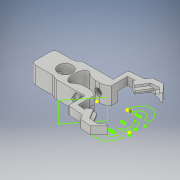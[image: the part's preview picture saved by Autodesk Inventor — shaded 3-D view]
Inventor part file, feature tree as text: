
AUTODESK INVENTOR PART (.ipt)
format: ipt  version: 2017 (Build 210142000, 142)  size: 1,308,160 bytes
history: native  units: in
note: dims shown in document units (in); Inventor stores cm internally (conversion verified against a paired STEP export)
features: sketch x38, projected_geometry x37, extrude x32, chamfer x8, plane x8, fillet x4, mirror x4, boolean_combine x3, move_body x3, split x2, revolve x1
ambient origin geometry x8: Origin, YZ Plane, XZ Plane, XY Plane, X Axis, Y Axis, Z Axis, Center Point
bodies: Solid2 (feature_tree), Solid4 (feature_tree), Solid5 (feature_tree), Solid6 (feature_tree), Solid7 (feature_tree), Solid8 (feature_tree)
feature tree (140):
  extrude  "Extrusion11"  Depth=0.1125in
  extrude  "Extrusion12"  Depth=0.0205in TaperAngle=0.0deg
  chamfer  "Chamfer17"  Distance=0.0627in Angle=45.0deg
  chamfer  "Chamfer18"  Distance=0.0627in Angle=45.0deg
  chamfer  "Chamfer19"  Distance=0.0627in Angle=45.0deg
  chamfer  "Chamfer20"  Distance=0.0627in Angle=45.0deg
  extrude  "Extrusion13"  Depth=0.0205in TaperAngle=0.0deg
  extrude  "Extrusion14"  Depth=0.0627in TaperAngle=45.0deg
  extrude  "Extrusion15"  Depth=0.0627in TaperAngle=45.0deg
  chamfer  "Chamfer21"  Distance=0.0627in Angle=45.0deg
  chamfer  "Chamfer22"  Distance=0.125in
  chamfer  "Chamfer23"  Distance=1.0in
  chamfer  "Chamfer24"  Distance=0.03in
  extrude  "Extrusion16"  Depth=0.03in
  fillet  "Fillet1"  [1 undecoded]
  extrude  "Extrusion17"  TaperAngle=90.0deg  [1 undecoded]
  fillet  "Fillet2"  Radius=0.03in
  extrude  "Extrusion18"  Depth=0.3in TaperAngle=0.0deg
  extrude  "Extrusion19"  Depth=1.0in TaperAngle=0.0deg
  extrude  "Extrusion22"  TaperAngle=90.0deg  [1 undecoded]
  extrude  "Extrusion25"  Depth=0.01in
  extrude  "Extrusion26"  Depth=0.5in
  revolve  "Revolution1"  [1 undecoded]
  plane  "Work Plane1"
  sketch  "Sketch33"  dims[d175=0.04in d176=1.0in d177=0.0in]
  sketch  "Sketch34"  dims[d179=0.06in d180=90.0deg]
  extrude  "Extrusion28"  Depth=0.185in TaperAngle=0.0deg
  boolean_combine  "Combine1"
  sketch  "Sketch35"  dims[d181=120.0deg d182=0.01in]
  plane  "Work Plane2"
  mirror  "Mirror1"
  extrude  "Extrusion29"  Depth=0.4119in TaperAngle=0.0deg
  extrude  "Extrusion30"  Depth=1.0in TaperAngle=0.0deg
  extrude  "Extrusion31"  Depth=0.13in
  extrude  "Extrusion32"  [1 undecoded]
  extrude  "Extrusion33"  Depth=0.13in TaperAngle=0.0deg
  extrude  "Extrusion34"  Depth=10.0in TaperAngle=0.0deg
  plane  "Work Plane3"
  extrude  "Extrusion35"  Depth=10.0in TaperAngle=0.0deg
  sketch  "Sketch44"  dims[d206=0.5in d207=0.0in d208=-0.12in]
  plane  "Work Plane5"
  split  "Split1"
  sketch  "Sketch45"  dims[d209=0.12in d210=0.13in d211=0.13in d212=0.0in]
  extrude  "Extrusion37"  Depth=10.0in TaperAngle=0.0deg
  move_body  "Move Body1"
  extrude  "Extrusion38"  Depth=0.1181in TaperAngle=0.0deg
  extrude  "Extrusion39"  Depth=0.1575in TaperAngle=0.0deg
  mirror  "Mirror2"
  extrude  "Extrusion40"  TaperAngle=90.0deg  [1 undecoded]
  extrude  "Extrusion41"  Depth=0.0394in TaperAngle=0.0deg
  extrude  "Extrusion42"  Depth=0.621in TaperAngle=0.0deg
  sketch  "Sketch52"  dims[d238=0.1969in d239=0.0in d240=0.0in d241=0.0in d242=0.0394in]
  boolean_combine  "Combine2"
  extrude  "Extrusion43"  Depth=1.0in TaperAngle=0.0deg
  extrude  "Extrusion44"  [1 undecoded]
  fillet  "Fillet3"  [1 undecoded]
  sketch  "Sketch54"  dims[d246=0.621in d247=0.0in d248=1.0in d249=0.0in]
  plane  "Work Plane6"
  extrude  "Extrusion45"  [1 undecoded]
  mirror  "Mirror3"
  plane  "Work Plane7"
  split  "Split2"
  move_body  "Move Body2"
  move_body  "Move Body3"
  plane  "Work Plane8"
  sketch  "Sketch56"
  extrude  "Extrusion46"  [1 undecoded]
  mirror  "Mirror4"
  boolean_combine  "Combine3"
  extrude  "Extrusion47"  [1 undecoded]
  extrude  "Extrusion48"  [1 undecoded]
  fillet  "Fillet4"  [1 undecoded]
  sketch  "Sketch1"  dims[d8=0.25in d83=0.1125in]
  sketch  "Sketch12"  dims[d84=0.02in d85=0.0in d86=0.0205in d87=0.0in d88=0.0627in d89=0.0205in d90=45.0deg d91=0.0627in d92=0.0205in d93=45.0deg d94=0.0627in d95=0.0205in d96=45.0deg d97=0.0627in d98=0.0205in d99=45.0deg]
  projected_geometry  "Projected Loop3"
  sketch  "Sketch14"  dims[d100=0.044in d101=0.0in d102=0.0205in d103=0.0in]
  projected_geometry  "Projected Loop4"
  sketch  "Sketch15"  dims[d104=0.02in d105=0.0in d106=0.0627in d107=0.0205in d108=45.0deg]
  projected_geometry  "Projected Loop5"
  projected_geometry  "Projected Loop6"
  sketch  "Sketch16"  dims[d109=0.0627in d110=0.0205in d111=45.0deg d112=0.0627in d113=0.0205in d114=45.0deg d115=0.0627in d116=0.0205in d117=45.0deg]
  projected_geometry  "Projected Loop7"
  sketch  "Sketch18"  dims[d119=0.45in d120=0.125in d121=0.0in]
  projected_geometry  "Projected Loop8"
  projected_geometry  "Projected Loop9"
  sketch  "Sketch19"  dims[d122=0.125in]
  projected_geometry  "Projected Loop10"
  projected_geometry  "Projected Loop11"
  projected_geometry  "Projected Loop12"
  projected_geometry  "Projected Loop13"
  sketch  "Sketch20"  dims[d123=0.3in]
  sketch  "Sketch21"  dims[d124=0.3in d125=1.0in d126=0.0in]
  sketch  "Sketch24"  dims[d127=0.1in d131=0.03in d132=0.0in]
  projected_geometry  "Projected Loop28"
  projected_geometry  "Projected Loop29"
  sketch  "Sketch29"  dims[d136=0.03in d137=0.0in d150=0.03in d151=90.0deg]
  sketch  "Sketch30"  dims[d152=0.03in d153=90.0deg d154=0.03in d155=0.0in]
  projected_geometry  "Projected Loop32"
  sketch  "Sketch31"  dims[d162=0.3in d169=1.0in d170=0.0in]
  projected_geometry  "Projected Loop33"
  projected_geometry  "Projected Loop36"
  projected_geometry  "Projected Loop37"
  projected_geometry  "Projected Loop38"
  projected_geometry  "Projected Loop39"
  projected_geometry  "Projected Loop40"
  projected_geometry  "Projected Loop41"
  projected_geometry  "Projected Loop42"
  projected_geometry  "Projected Loop43"
  sketch  "Sketch36"  dims[d183=0.01in d184=0.5in]
  sketch  "Sketch37"  dims[d187=0.185in d188=0.0in d190=0.0197in]
  projected_geometry  "Projected Loop44"
  sketch  "Sketch38"  dims[d192=0.6644in d193=0.185in d194=0.0in]
  projected_geometry  "Projected Loop45"
  sketch  "Sketch39"  dims[d195=1.0in d196=0.0in d197=0.4119in d198=0.0in]
  sketch  "Sketch40"  dims[d199=0.07in d200=0.0in d201=1.0in d202=0.0in]
  sketch  "Sketch41"  dims[d203=0.12in d205=0.13in]
  plane  "Work Plane4"
  sketch  "Sketch46"  dims[d215=-0.097in d216=10.0in d217=0.0in]
  sketch  "Sketch47"  dims[d218=0.0in d219=0.0in d220=0.0394in d221=10.0in d222=0.0in]
  sketch  "Sketch48"  dims[d223=0.0in d224=0.0in d226=10.0in d227=0.0in]
  sketch  "Sketch49"  dims[d228=0.1181in d229=0.0in d230=0.1181in d231=0.0in]
  sketch  "Sketch50"  dims[d232=0.1575in d233=0.0in d234=0.1575in d235=0.0in]
  projected_geometry  "Projected Loop46"
  projected_geometry  "Projected Loop47"
  projected_geometry  "Projected Loop48"
  sketch  "Sketch51"  dims[d236=0.125in d237=90.0deg]
  projected_geometry  "Projected Loop49"
  projected_geometry  "Projected Loop50"
  sketch  "Sketch53"  dims[d243=0.0344in d244=0.621in d245=0.0in]
  projected_geometry  "Projected Loop51"
  projected_geometry  "Projected Loop52"
  projected_geometry  "Projected Loop53"
  sketch  "Sketch55"  dims[d250=0.3in]
  projected_geometry  "Projected Loop54"
  sketch  "Sketch57"
  sketch  "Sketch58"
  projected_geometry  "Projected Loop55"
  projected_geometry  "Projected Loop56"
  sketch  "Sketch59"
  projected_geometry  "Projected Loop57"
note: 13 required parameter values undecoded (feature->parameter linkage not recoverable at this tier; creation-order binding heuristic only, values carry confidence <= 0.55)